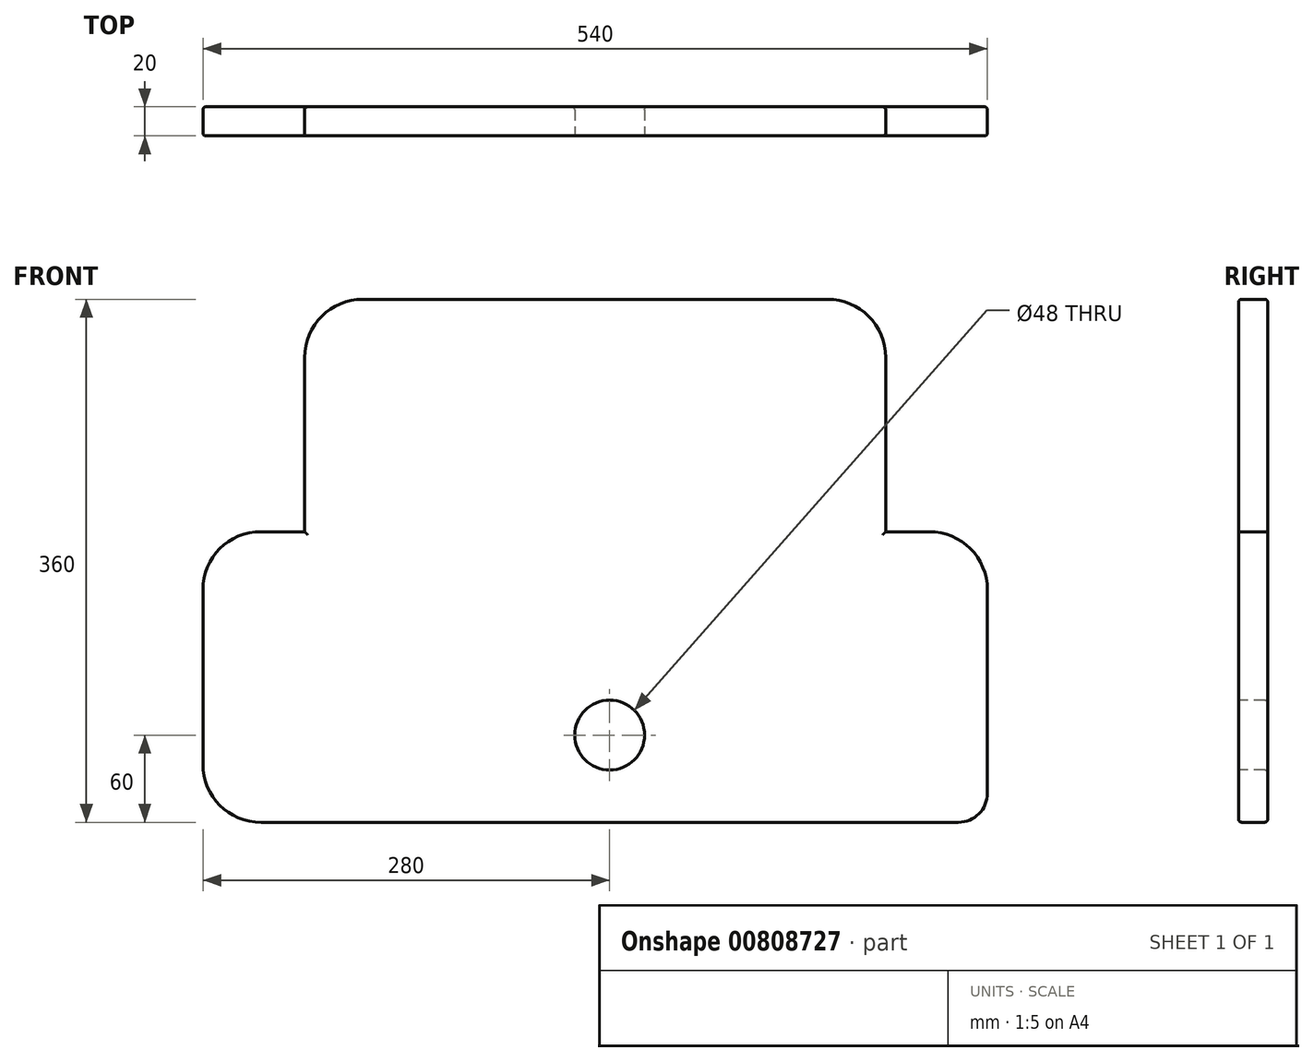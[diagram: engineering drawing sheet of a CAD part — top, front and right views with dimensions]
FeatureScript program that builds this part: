
annotation { "Feature Type Name" : "Feature", "Feature Type Description" : "" }
export const myFeature = defineFeature(function(context is Context, id is Id, definition is map)
    precondition{}
    {
        {
            var Q0;
            Q0=qCreatedBy(makeId("Front.planeOp"),FACE);
            var sketch = newSketch(context, id + "F0", { "sketchPlane" : qUnion([Q0])});
            skLineSegment(sketch, "E0.bottom", {"start": v(250, -180) * mm, "end": v(-230, -180) * mm});
            skLineSegment(sketch, "E0.top", {"start": v(200, 180) * mm, "end": v(-200, 180) * mm});
            skLineSegment(sketch, "E0.left", {"start": v(270, -160) * mm, "end": v(270, -20) * mm});
            skLineSegment(sketch, "E0.right", {"start": v(-270, -140) * mm, "end": v(-270, -20) * mm});
            skPoint(sketch, "E0.middle", {"position": v(0, 0) * mm});
            skLineSegment(sketch, "E1", {"start": v(-230, 20) * mm, "end": v(-200, 20) * mm});
            skLineSegment(sketch, "E2", {"start": v(-200, 20) * mm, "end": v(-200, 140) * mm});
            skPoint(sketch, "E3.orphan", {"position": v(-270, 180) * mm});
            skLineSegment(sketch, "E4.MirrorCS", {"start": v(230, 20) * mm, "end": v(200, 20) * mm});
            skLineSegment(sketch, "E5.MirrorCS", {"start": v(200, 20) * mm, "end": v(200, 140) * mm});
            skLineSegment(sketch, "E6.MirrorCS", {"start": v(-160, 180) * mm, "end": v(160, 180) * mm});
            skPoint(sketch, "E7.orphan", {"position": v(270, 180) * mm});
            skPoint(sketch, "E8.visualSharp", {"position": v(-200, 180) * mm});
            skArc(sketch, "E8.filletArc", {"start": v(-160, 180) * mm, "mid": v(-188.28, 168.28) * mm, "end": v(-200, 140) * mm});
            skPoint(sketch, "E9.visualSharp", {"position": v(200, 180) * mm});
            skArc(sketch, "E9.filletArc", {"start": v(200, 140) * mm, "mid": v(188.28, 168.28) * mm, "end": v(160, 180) * mm});
            skPoint(sketch, "E10.visualSharp", {"position": v(270, 20) * mm});
            skArc(sketch, "E10.filletArc", {"start": v(270, -20) * mm, "mid": v(258.28, 8.28) * mm, "end": v(230, 20) * mm});
            skPoint(sketch, "E11.visualSharp", {"position": v(270, -180) * mm});
            skArc(sketch, "E11.filletArc", {"start": v(250, -180) * mm, "mid": v(264.14, -174.14) * mm, "end": v(270, -160) * mm});
            skPoint(sketch, "E12.visualSharp", {"position": v(-270, -180) * mm});
            skArc(sketch, "E12.filletArc", {"start": v(-270, -140) * mm, "mid": v(-258.28, -168.28) * mm, "end": v(-230, -180) * mm});
            skPoint(sketch, "E13.visualSharp", {"position": v(-270, 20) * mm});
            skArc(sketch, "E13.filletArc", {"start": v(-230, 20) * mm, "mid": v(-258.28, 8.28) * mm, "end": v(-270, -20) * mm});
            skSolve(sketch);
        }
        {
            var Q0;
            Q0=makeQuery(id+"F0.imprint","IMPRINT",FACE,{"disambiguationData":[TD([[makeQuery(id+"F0.imprint","IMPRINT",EDGE,{"derivedFrom":sQuery(id+"F0.wireOp",EDGE,"E0.bottom")}),-1.0]])]});
            extrude(context, id + "F1", {"entities" : qUnion([Q0]), "depth" : 20 * mm, "offsetDistance" : 25 * mm});
        }
        {
            var Q0;
            Q0=makeQuery(id+"F1.opExtrude","CAP_FACE",FACE,{"disambiguationData":[OSD([sQuery(id+"F0.wireOp",EDGE,"E0.bottom"),sQuery(id+"F0.wireOp",EDGE,"E0.left"),sQuery(id+"F0.wireOp",EDGE,"E0.right"),sQuery(id+"F0.wireOp",EDGE,"E1"),sQuery(id+"F0.wireOp",EDGE,"E2"),sQuery(id+"F0.wireOp",EDGE,"E4.MirrorCS"),sQuery(id+"F0.wireOp",EDGE,"E5.MirrorCS"),sQuery(id+"F0.wireOp",EDGE,"E6.MirrorCS"),sQuery(id+"F0.wireOp",EDGE,"E8.filletArc"),sQuery(id+"F0.wireOp",EDGE,"E9.filletArc"),sQuery(id+"F0.wireOp",EDGE,"E10.filletArc"),sQuery(id+"F0.wireOp",EDGE,"E11.filletArc"),sQuery(id+"F0.wireOp",EDGE,"E12.filletArc"),sQuery(id+"F0.wireOp",EDGE,"E13.filletArc")])],"isStart":false});
            var sketch = newSketch(context, id + "F2", { "sketchPlane" : qUnion([Q0])});
            skLineSegment(sketch, "E14", {"start": v(-200, 20) * mm, "end": v(-209, 20) * mm, "construction": true});
            skLineSegment(sketch, "E15", {"start": v(-209, 20) * mm, "end": v(-209, -180) * mm, "construction": true});
            skPoint(sketch, "E16", {"position": v(-209, -80) * mm});
            skPoint(sketch, "E17.MirrorP", {"position": v(209, -80) * mm});
            skSolve(sketch);
        }
        {
            var Q0;
            Q0=makeQuery(id+"F1.opExtrude","CAP_FACE",FACE,{"disambiguationData":[OSD([sQuery(id+"F0.wireOp",EDGE,"E0.bottom"),sQuery(id+"F0.wireOp",EDGE,"E0.left"),sQuery(id+"F0.wireOp",EDGE,"E0.right"),sQuery(id+"F0.wireOp",EDGE,"E1"),sQuery(id+"F0.wireOp",EDGE,"E2"),sQuery(id+"F0.wireOp",EDGE,"E4.MirrorCS"),sQuery(id+"F0.wireOp",EDGE,"E5.MirrorCS"),sQuery(id+"F0.wireOp",EDGE,"E6.MirrorCS"),sQuery(id+"F0.wireOp",EDGE,"E8.filletArc"),sQuery(id+"F0.wireOp",EDGE,"E9.filletArc"),sQuery(id+"F0.wireOp",EDGE,"E10.filletArc"),sQuery(id+"F0.wireOp",EDGE,"E11.filletArc"),sQuery(id+"F0.wireOp",EDGE,"E12.filletArc"),sQuery(id+"F0.wireOp",EDGE,"E13.filletArc")])],"isStart":false});
            var Q1;
            Q1=makeQuery(id+"F1.opExtrude","CAP_FACE",FACE,{"disambiguationData":[OSD([sQuery(id+"F0.wireOp",EDGE,"E0.bottom"),sQuery(id+"F0.wireOp",EDGE,"E0.left"),sQuery(id+"F0.wireOp",EDGE,"E0.right"),sQuery(id+"F0.wireOp",EDGE,"E1"),sQuery(id+"F0.wireOp",EDGE,"E2"),sQuery(id+"F0.wireOp",EDGE,"E4.MirrorCS"),sQuery(id+"F0.wireOp",EDGE,"E5.MirrorCS"),sQuery(id+"F0.wireOp",EDGE,"E6.MirrorCS"),sQuery(id+"F0.wireOp",EDGE,"E8.filletArc"),sQuery(id+"F0.wireOp",EDGE,"E9.filletArc"),sQuery(id+"F0.wireOp",EDGE,"E10.filletArc"),sQuery(id+"F0.wireOp",EDGE,"E11.filletArc"),sQuery(id+"F0.wireOp",EDGE,"E12.filletArc"),sQuery(id+"F0.wireOp",EDGE,"E13.filletArc")])],"isStart":true});
            fillet(context, id + "F3", {"entities" : qUnion([Q0, Q1]), "radius" : 2 * mm, "tangentPropagation" : true, "allowEdgeOverflow" : false});
        }
        {
            var Q0;
            Q0=makeQuery(id+"F2.imprint","IMPRINT",FACE,{"disambiguationData":[TD([[makeQuery(id+"F2.imprint","IMPRINT",EDGE,{"derivedFrom":makeQuery(id+"F1.opExtrude","CAP_EDGE",EDGE,{"disambiguationData":[OSD([sQuery(id+"F0.wireOp",EDGE,"E0.bottom")])],"isStart":false})}),-1.0]])]});
            var sketch = newSketch(context, id + "F4", { "sketchPlane" : qUnion([Q0])});
            skLineSegment(sketch, "E18", {"start": v(10, -180) * mm, "end": v(10, -120) * mm, "construction": true});
            skPoint(sketch, "E19.orphan", {"position": v(-230, -180) * mm});
            skPoint(sketch, "E20.0.start.orphan", {"position": v(250, -180) * mm});
            skCircle(sketch, "E21", {"center": v(10, -120) * mm, "radius": 24 * mm});
            skLineSegment(sketch, "E22", {"start": v(-14, -120) * mm, "end": v(-29.91, -120) * mm});
            skPoint(sketch, "E23", {"position": v(-29.91, -120) * mm});
            skSolve(sketch);
        }
        {
            var Q0;
            Q0=makeQuery(id+"F4.imprint","IMPRINT",FACE,{"disambiguationData":[TD([[makeQuery(id+"F4.imprint","IMPRINT",EDGE,{"derivedFrom":sQuery(id+"F4.wireOp",EDGE,"E21")}),1.0]])]});
            extrude(context, id + "F5", {"entities" : qUnion([Q0]), "operationType" : NewBodyOperationType.REMOVE, "oppositeDirection" : true, "depth" : 25 * mm, "offsetDistance" : 25 * mm});
        }
        {
            var Q0;
            Q0=makeQuery(id+"F5.boolean.opBoolean","COPY",EDGE,{"derivedFrom":makeQuery(id+"F5.opExtrude","CAP_EDGE",EDGE,{"disambiguationData":[OSD([sQuery(id+"F4.wireOp",EDGE,"E21")])],"isStart":true})});
            var Q1;
            Q1=makeQuery(id+"F5.boolean.opBoolean","INTERSECT",EDGE,{"derivedFrom":[makeQuery(id+"F1.opExtrude","CAP_FACE",FACE,{"disambiguationData":[OSD([sQuery(id+"F0.wireOp",EDGE,"E0.bottom"),sQuery(id+"F0.wireOp",EDGE,"E0.left"),sQuery(id+"F0.wireOp",EDGE,"E0.right"),sQuery(id+"F0.wireOp",EDGE,"E1"),sQuery(id+"F0.wireOp",EDGE,"E2"),sQuery(id+"F0.wireOp",EDGE,"E4.MirrorCS"),sQuery(id+"F0.wireOp",EDGE,"E5.MirrorCS"),sQuery(id+"F0.wireOp",EDGE,"E6.MirrorCS"),sQuery(id+"F0.wireOp",EDGE,"E8.filletArc"),sQuery(id+"F0.wireOp",EDGE,"E9.filletArc"),sQuery(id+"F0.wireOp",EDGE,"E10.filletArc"),sQuery(id+"F0.wireOp",EDGE,"E11.filletArc"),sQuery(id+"F0.wireOp",EDGE,"E12.filletArc"),sQuery(id+"F0.wireOp",EDGE,"E13.filletArc")])],"isStart":true}),makeQuery(id+"F5.opExtrude","SWEPT_FACE",FACE,{"disambiguationData":[OSD([sQuery(id+"F4.wireOp",EDGE,"E21")])]})]});
            fillet(context, id + "F6", {"entities" : qUnion([Q0, Q1]), "radius" : 2 * mm, "tangentPropagation" : true, "allowEdgeOverflow" : false});
        }
    });
